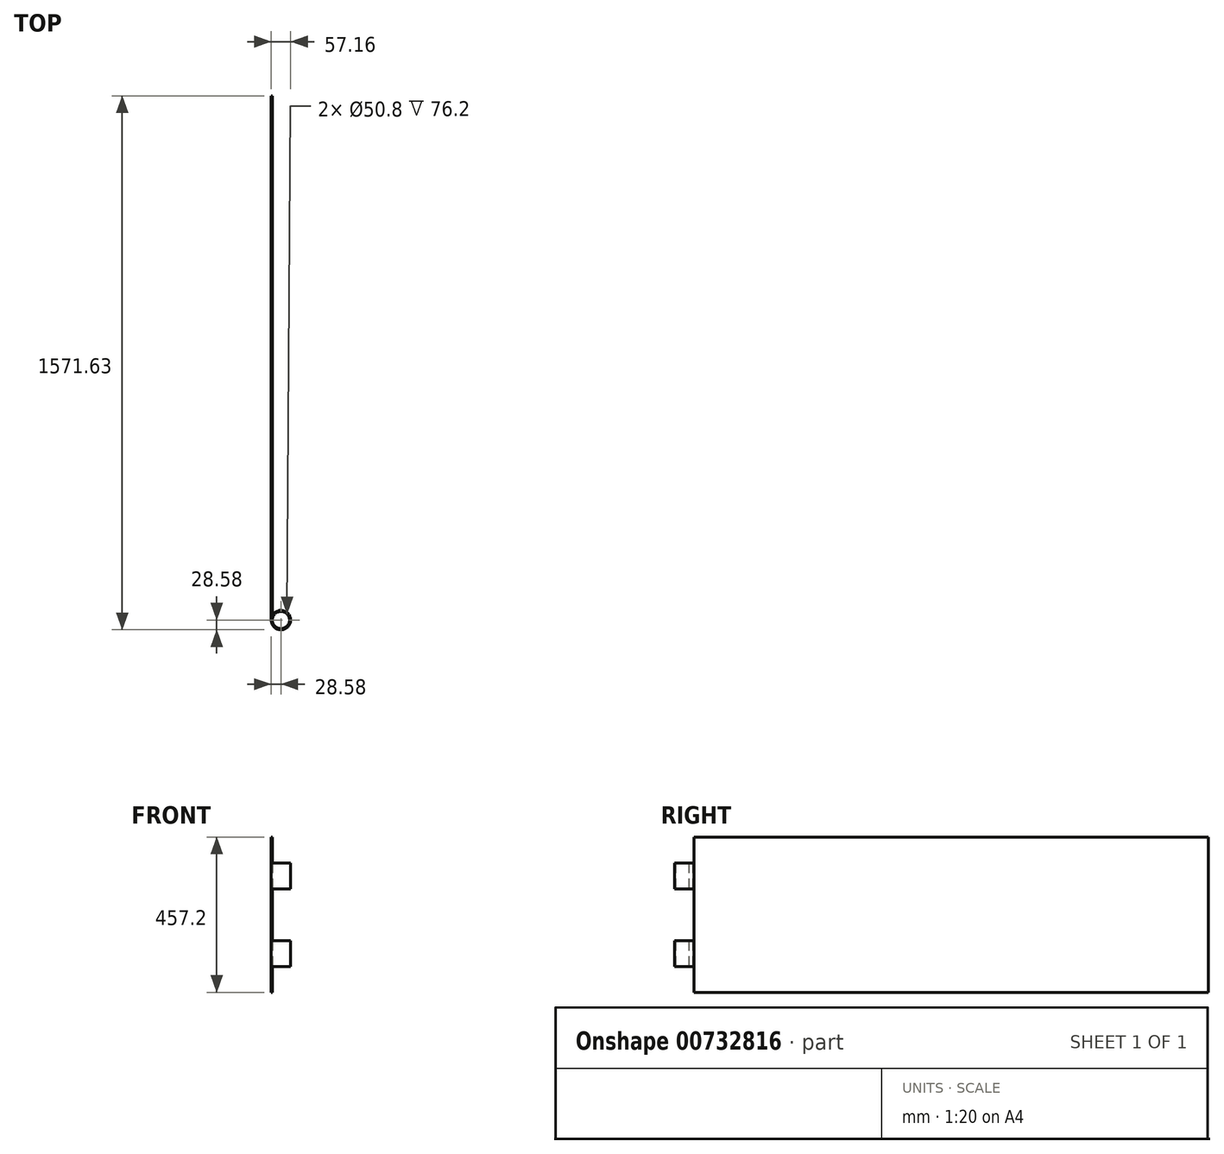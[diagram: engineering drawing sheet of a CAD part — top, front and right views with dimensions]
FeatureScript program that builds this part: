
annotation { "Feature Type Name" : "Feature", "Feature Type Description" : "" }
export const myFeature = defineFeature(function(context is Context, id is Id, definition is map)
    precondition{}
    {
        {
            var Q0;
            Q0=qCreatedBy(makeId("Top.planeOp"),FACE);
            var sketch = newSketch(context, id + "F0", { "sketchPlane" : qUnion([Q0])});
            skCircle(sketch, "E0", {"center": v(0, 0) * mm, "radius": 25.4 * mm});
            skArc(sketch, "E1.0", {"start": v(-28.58, 0) * mm, "mid": v(27.77, -6.74) * mm, "end": v(-25.4, 13.1) * mm});
            skLineSegment(sketch, "E2.top", {"start": v(-28.58, 800.1) * mm, "end": v(-25.4, 800.1) * mm});
            skLineSegment(sketch, "E2.left", {"start": v(-28.58, 0) * mm, "end": v(-28.58, 800.1) * mm});
            skLineSegment(sketch, "E2.right", {"start": v(-25.4, 13.1) * mm, "end": v(-25.4, 800.1) * mm});
            skSolve(sketch);
        }
        {
            var Q0;
            Q0=qSketchRegion(id+"F0",true);
            extrude(context, id + "F1", {"entities" : qUnion([Q0]), "depth" : 457.2 * mm, "offsetDistance" : 25.4 * mm});
        }
        {
            var Q0;
            Q0=qCreatedBy(makeId("Right.planeOp"),FACE);
            var sketch = newSketch(context, id + "F2", { "sketchPlane" : qUnion([Q0])});
            skLineSegment(sketch, "E3.bottom", {"start": v(28.57, 381) * mm, "end": v(-28.58, 381) * mm});
            skLineSegment(sketch, "E3.top", {"start": v(28.57, 304.8) * mm, "end": v(-28.58, 304.8) * mm});
            skLineSegment(sketch, "E3.right", {"start": v(-28.58, 381) * mm, "end": v(-28.58, 304.8) * mm});
            skPoint(sketch, "E3.middle", {"position": v(0, 342.9) * mm});
            skLineSegment(sketch, "E4.bottom", {"start": v(28.57, 152.4) * mm, "end": v(-28.57, 152.4) * mm});
            skLineSegment(sketch, "E4.top", {"start": v(28.57, 76.2) * mm, "end": v(-28.58, 76.2) * mm});
            skLineSegment(sketch, "E4.right", {"start": v(-28.58, 152.4) * mm, "end": v(-28.58, 76.2) * mm});
            skPoint(sketch, "E4.middle", {"position": v(0, 114.3) * mm});
            skLineSegment(sketch, "E5.top", {"start": v(28.57, 460.44) * mm, "end": v(-28.58, 460.44) * mm});
            skLineSegment(sketch, "E5.left", {"start": v(28.57, 381) * mm, "end": v(28.57, 460.44) * mm});
            skLineSegment(sketch, "E5.right", {"start": v(-28.58, 381) * mm, "end": v(-28.58, 460.44) * mm});
            skLineSegment(sketch, "E6.bottom", {"start": v(28.57, 304.8) * mm, "end": v(-28.57, 304.8) * mm});
            skLineSegment(sketch, "E6.left", {"start": v(28.57, 304.8) * mm, "end": v(28.57, 152.4) * mm});
            skLineSegment(sketch, "E6.right", {"start": v(-28.57, 304.8) * mm, "end": v(-28.57, 152.4) * mm});
            skPoint(sketch, "E7.oppositeSnap0", {"position": v(-28.57, 228.6) * mm});
            skLineSegment(sketch, "E7.bottom", {"start": v(28.57, 76.2) * mm, "end": v(-28.57, 76.2) * mm});
            skLineSegment(sketch, "E7.top", {"start": v(28.57, 0) * mm, "end": v(-28.57, 0) * mm});
            skLineSegment(sketch, "E7.left", {"start": v(28.57, 76.2) * mm, "end": v(28.57, 0) * mm});
            skLineSegment(sketch, "E7.right", {"start": v(-28.57, 76.2) * mm, "end": v(-28.57, 0) * mm});
            skSolve(sketch);
        }
        {
            var Q0;
            Q0=qSketchRegion(id+"F2",true);
            extrude(context, id + "F3", {"entities" : qUnion([Q0]), "operationType" : NewBodyOperationType.REMOVE, "endBound" : BoundingType.THROUGH_ALL, "oppositeDirection" : true, "depth" : 25.4 * mm, "offsetDistance" : 25.4 * mm, "hasSecondDirection" : true, "secondDirectionBound" : BoundingType.THROUGH_ALL, "secondDirectionOppositeDirection" : false, "secondDirectionDepth" : 25.4 * mm});
        }
        {
            var Q0;
            Q0=makeQuery(id+"F1.opExtrude","SWEPT_FACE",FACE,{"disambiguationData":[OSD([sQuery(id+"F0.wireOp",EDGE,"E2.top")])]});
            var sketch = newSketch(context, id + "F4", { "sketchPlane" : qUnion([Q0])});
            skLineSegment(sketch, "E8.bottom", {"start": v(25.4, 457.2) * mm, "end": v(28.58, 457.2) * mm});
            skLineSegment(sketch, "E8.top", {"start": v(25.4, 0) * mm, "end": v(28.58, 0) * mm});
            skLineSegment(sketch, "E8.left", {"start": v(25.4, 457.2) * mm, "end": v(25.4, 0) * mm});
            skLineSegment(sketch, "E8.right", {"start": v(28.58, 457.2) * mm, "end": v(28.58, 0) * mm});
            skSolve(sketch);
        }
        {
            var Q0;
            Q0 = qSketchRegion(id + "F4", true);
            extrude(context, id + "F5", {"entities" : qUnion([Q0]), "operationType" : NewBodyOperationType.ADD, "depth" : 742.95 * mm, "offsetDistance" : 25.4 * mm});
        }
    });
